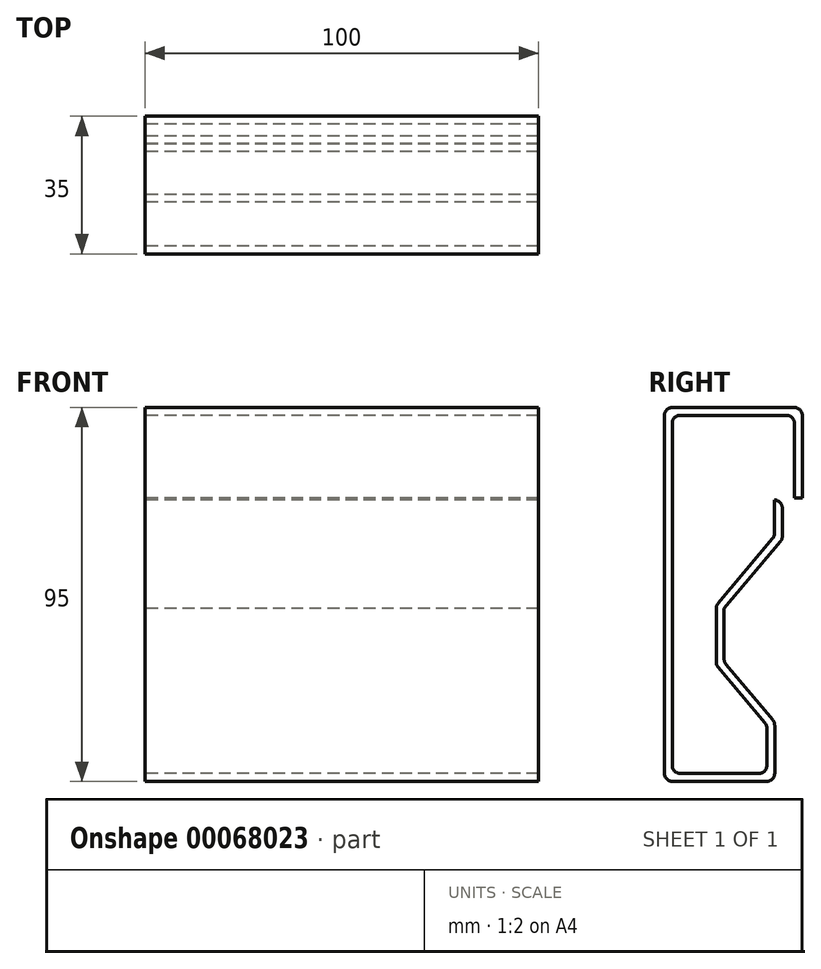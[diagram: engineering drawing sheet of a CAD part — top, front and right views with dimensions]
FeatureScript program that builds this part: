
annotation { "Feature Type Name" : "Feature", "Feature Type Description" : "" }
export const myFeature = defineFeature(function(context is Context, id is Id, definition is map)
    precondition{}
    {
        {
            var Q0;
            Q0=qCreatedBy(makeId("Right.planeOp"),FACE);
            var sketch = newSketch(context, id + "F0", { "sketchPlane" : qUnion([Q0])});
            skLineSegment(sketch, "E0", {"start": v(35, -23) * mm, "end": v(35, 0) * mm});
            skLineSegment(sketch, "E1", {"start": v(35, 0) * mm, "end": v(0, 0) * mm});
            skLineSegment(sketch, "E2", {"start": v(0, 0) * mm, "end": v(0, -95) * mm});
            skLineSegment(sketch, "E3", {"start": v(0, -95) * mm, "end": v(28, -95) * mm});
            skLineSegment(sketch, "E4", {"start": v(33, -23) * mm, "end": v(35, -23) * mm});
            skLineSegment(sketch, "E5.1", {"start": v(2, -2) * mm, "end": v(2, -93) * mm});
            skLineSegment(sketch, "E5.2", {"start": v(33, -2) * mm, "end": v(2, -2) * mm});
            skLineSegment(sketch, "E5.3", {"start": v(33, -23) * mm, "end": v(33, -2) * mm});
            skLineSegment(sketch, "E6", {"start": v(28, -95) * mm, "end": v(28, -80) * mm});
            skLineSegment(sketch, "E7", {"start": v(28, -80) * mm, "end": v(15.14, -64.68) * mm});
            skLineSegment(sketch, "E8", {"start": v(29.93, -33.52) * mm, "end": v(29.93, -23.52) * mm});
            skLineSegment(sketch, "E9.0", {"start": v(27.93, -32.79) * mm, "end": v(27.93, -23.52) * mm});
            skLineSegment(sketch, "E9.1", {"start": v(2, -93) * mm, "end": v(26, -93) * mm});
            skLineSegment(sketch, "E9.2", {"start": v(26, -93) * mm, "end": v(26, -80.73) * mm});
            skLineSegment(sketch, "E9.3", {"start": v(26, -80.73) * mm, "end": v(13.14, -65.4) * mm});
            skLineSegment(sketch, "E9.4", {"start": v(13.14, -50.4) * mm, "end": v(27.93, -32.79) * mm});
            skLineSegment(sketch, "E10", {"start": v(29.93, -23.52) * mm, "end": v(27.93, -23.52) * mm});
            skLineSegment(sketch, "E11", {"start": v(13.14, -65.4) * mm, "end": v(13.14, -50.4) * mm});
            skLineSegment(sketch, "E12", {"start": v(15.14, -64.68) * mm, "end": v(15.14, -51.13) * mm});
            skLineSegment(sketch, "E13.trimOffspring", {"start": v(15.14, -51.13) * mm, "end": v(29.93, -33.52) * mm});
            skSolve(sketch);
        }
        {
            var Q0;
            Q0=makeQuery(id+"F0.imprint","IMPRINT",FACE,{"disambiguationData":[TD([[makeQuery(id+"F0.imprint","IMPRINT",EDGE,{"derivedFrom":sQuery(id+"F0.wireOp",EDGE,"E0")}),1.0]])]});
            extrude(context, id + "F1", {"entities" : qUnion([Q0]), "depth" : 100 * mm});
        }
        {
            var Q0;
            Q0=makeQuery(id+"F1.opExtrude","SWEPT_EDGE",EDGE,{"disambiguationData":[OSD([sQuery(id+"F0.wireOp",EDGE,"E0"),sQuery(id+"F0.wireOp",EDGE,"E1")])]});
            var Q1;
            Q1=makeQuery(id+"F1.opExtrude","SWEPT_EDGE",EDGE,{"disambiguationData":[OSD([sQuery(id+"F0.wireOp",EDGE,"E1"),sQuery(id+"F0.wireOp",EDGE,"E2")])]});
            var Q2;
            Q2=makeQuery(id+"F1.opExtrude","SWEPT_EDGE",EDGE,{"disambiguationData":[OSD([sQuery(id+"F0.wireOp",EDGE,"E5.2"),sQuery(id+"F0.wireOp",EDGE,"E5.3")])]});
            var Q3;
            Q3=makeQuery(id+"F1.opExtrude","SWEPT_EDGE",EDGE,{"disambiguationData":[OSD([sQuery(id+"F0.wireOp",EDGE,"E5.1"),sQuery(id+"F0.wireOp",EDGE,"E5.2")])]});
            var Q4;
            Q4=makeQuery(id+"F1.opExtrude","SWEPT_EDGE",EDGE,{"disambiguationData":[OSD([sQuery(id+"F0.wireOp",EDGE,"E2"),sQuery(id+"F0.wireOp",EDGE,"E3")])]});
            var Q5;
            Q5=makeQuery(id+"F1.opExtrude","SWEPT_EDGE",EDGE,{"disambiguationData":[OSD([sQuery(id+"F0.wireOp",EDGE,"E3"),sQuery(id+"F0.wireOp",EDGE,"E6")])]});
            var Q6;
            Q6=makeQuery(id+"F1.opExtrude","SWEPT_EDGE",EDGE,{"disambiguationData":[OSD([sQuery(id+"F0.wireOp",EDGE,"E6"),sQuery(id+"F0.wireOp",EDGE,"E7")])]});
            var Q7;
            Q7=makeQuery(id+"F1.opExtrude","SWEPT_EDGE",EDGE,{"disambiguationData":[OSD([sQuery(id+"F0.wireOp",EDGE,"E7"),sQuery(id+"F0.wireOp",EDGE,"flTL06ic-Ythc-fAiD-JKfi-vYeBe5ndK5os")])]});
            var Q8;
            Q8=makeQuery(id+"F1.opExtrude","SWEPT_EDGE",EDGE,{"disambiguationData":[OSD([sQuery(id+"F0.wireOp",EDGE,"flTL06ic-Ythc-fAiD-JKfi-vYeBe5ndK5os"),sQuery(id+"F0.wireOp",EDGE,"E8")])]});
            var Q9;
            Q9=makeQuery(id+"F1.opExtrude","SWEPT_EDGE",EDGE,{"disambiguationData":[OSD([sQuery(id+"F0.wireOp",EDGE,"E5.1"),sQuery(id+"F0.wireOp",EDGE,"E9.1")])]});
            var Q10;
            Q10=makeQuery(id+"F1.opExtrude","SWEPT_EDGE",EDGE,{"disambiguationData":[OSD([sQuery(id+"F0.wireOp",EDGE,"E9.1"),sQuery(id+"F0.wireOp",EDGE,"E9.2")])]});
            var Q11;
            Q11=makeQuery(id+"F1.opExtrude","SWEPT_EDGE",EDGE,{"disambiguationData":[OSD([sQuery(id+"F0.wireOp",EDGE,"E9.2"),sQuery(id+"F0.wireOp",EDGE,"E9.3")])]});
            var Q12;
            Q12=makeQuery(id+"F1.opExtrude","SWEPT_EDGE",EDGE,{"disambiguationData":[OSD([sQuery(id+"F0.wireOp",EDGE,"E9.3"),sQuery(id+"F0.wireOp",EDGE,"E9.4")])]});
            var Q13;
            Q13=makeQuery(id+"F1.opExtrude","SWEPT_EDGE",EDGE,{"disambiguationData":[OSD([sQuery(id+"F0.wireOp",EDGE,"E9.0"),sQuery(id+"F0.wireOp",EDGE,"E9.4")])]});
            fillet(context, id + "F2", {"entities" : qUnion([Q0, Q1, Q2, Q3, Q4, Q5, Q6, Q7, Q8, Q9, Q10, Q11, Q12, Q13]), "radius" : 2 * mm, "tangentPropagation" : true, "allowEdgeOverflow" : false});
        }
    });
